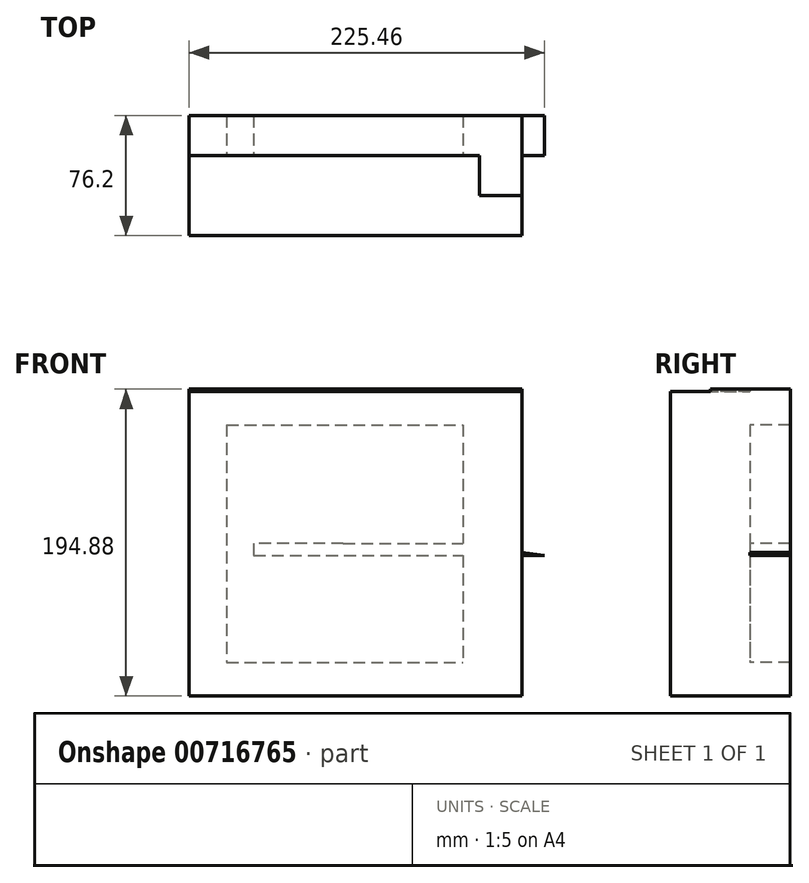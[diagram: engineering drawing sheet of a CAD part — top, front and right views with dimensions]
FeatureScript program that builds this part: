
annotation { "Feature Type Name" : "Feature", "Feature Type Description" : "" }
export const myFeature = defineFeature(function(context is Context, id is Id, definition is map)
    precondition{}
    {
        {
            var Q0;
            Q0=qCreatedBy(makeId("Front.planeOp"),FACE);
            var sketch = newSketch(context, id + "F0", { "sketchPlane" : qUnion([Q0])});
            skLineSegment(sketch, "E0.bottom", {"start": v(-97.79, 96.41) * mm, "end": v(96, 96.41) * mm});
            skLineSegment(sketch, "E0.top", {"start": v(-97.79, -96.95) * mm, "end": v(96, -96.95) * mm});
            skLineSegment(sketch, "E0.left", {"start": v(-97.79, 96.41) * mm, "end": v(-97.79, -96.95) * mm});
            skLineSegment(sketch, "E0.right", {"start": v(96, 96.41) * mm, "end": v(96, -96.95) * mm});
            skSolve(sketch);
        }
        {
            var Q0;
            Q0 = qSketchRegion(id + "F0", true);
            extrude(context, id + "F1", {"entities" : qUnion([Q0]), "depth" : 25.4 * mm, "offsetDistance" : 25.4 * mm});
        }
        {
            var Q0;
            Q0=makeQuery(id+"F1.opExtrude","CAP_FACE",FACE,{"disambiguationData":[OSD([sQuery(id+"F0.wireOp",EDGE,"E0.bottom"),sQuery(id+"F0.wireOp",EDGE,"E0.top"),sQuery(id+"F0.wireOp",EDGE,"E0.left"),sQuery(id+"F0.wireOp",EDGE,"E0.right")])],"isStart":false});
            var sketch = newSketch(context, id + "F2", { "sketchPlane" : qUnion([Q0])});
            skLineSegment(sketch, "E1.bottom", {"start": v(-97.79, -96.95) * mm, "end": v(88.13, -96.95) * mm});
            skLineSegment(sketch, "E1.top", {"start": v(-97.79, 96.41) * mm, "end": v(88.13, 96.41) * mm});
            skLineSegment(sketch, "E1.left", {"start": v(-97.79, -96.95) * mm, "end": v(-97.79, 96.41) * mm});
            skLineSegment(sketch, "E1.right", {"start": v(88.13, -96.95) * mm, "end": v(88.13, 96.41) * mm});
            skSolve(sketch);
        }
        {
            var Q0;
            Q0 = qSketchRegion(id + "F2", true);
            extrude(context, id + "F3", {"entities" : qUnion([Q0]), "operationType" : NewBodyOperationType.ADD, "depth" : 25.4 * mm, "offsetDistance" : 25.4 * mm});
        }
        {
            var Q0;
            Q0=makeQuery(id+"F3.opExtrude","SWEPT_FACE",FACE,{"disambiguationData":[OSD([sQuery(id+"F2.wireOp",EDGE,"E1.right")])]});
            var sketch = newSketch(context, id + "F4", { "sketchPlane" : qUnion([Q0])});
            skLineSegment(sketch, "E2.bottom", {"start": v(-50.8, 96.41) * mm, "end": v(-25.4, 96.41) * mm});
            skLineSegment(sketch, "E2.top", {"start": v(-50.8, -96.95) * mm, "end": v(-25.4, -96.95) * mm});
            skLineSegment(sketch, "E2.left", {"start": v(-50.8, 96.41) * mm, "end": v(-50.8, -96.95) * mm});
            skLineSegment(sketch, "E2.right", {"start": v(-25.4, 96.41) * mm, "end": v(-25.4, -96.95) * mm});
            skSolve(sketch);
        }
        {
            var Q0;
            Q0 = qSketchRegion(id + "F4", true);
            extrude(context, id + "F5", {"entities" : qUnion([Q0]), "operationType" : NewBodyOperationType.ADD, "depth" : 25.4 * mm, "offsetDistance" : 25.4 * mm});
        }
        {
            var Q0;
            Q0=makeQuery(id+"F5.opExtrude","SWEPT_FACE",FACE,{"disambiguationData":[OSD([sQuery(id+"F4.wireOp",EDGE,"E2.right")])]});
            var sketch = newSketch(context, id + "F6", { "sketchPlane" : qUnion([Q0])});
            skLineSegment(sketch, "E3.bottom", {"start": v(-86.6, 97.93) * mm, "end": v(-113.53, 97.93) * mm});
            skLineSegment(sketch, "E3.top", {"start": v(-86.6, -96.95) * mm, "end": v(-113.53, -96.95) * mm});
            skLineSegment(sketch, "E3.left", {"start": v(-86.6, 97.93) * mm, "end": v(-86.6, -96.95) * mm});
            skLineSegment(sketch, "E3.right", {"start": v(-113.53, 97.93) * mm, "end": v(-113.53, -96.95) * mm});
            skSolve(sketch);
        }
        {
            var Q0;
            Q0 = qSketchRegion(id + "F6", true);
            extrude(context, id + "F7", {"entities" : qUnion([Q0]), "operationType" : NewBodyOperationType.ADD, "depth" : 25.4 * mm, "offsetDistance" : 25.4 * mm});
        }
        {
            var Q0;
            Q0=makeQuery(id+"F7.boolean.opBoolean","MERGE",FACE,{"derivedFrom":[makeQuery(id+"F1.opExtrude","CAP_FACE",FACE,{"disambiguationData":[OSD([sQuery(id+"F0.wireOp",EDGE,"E0.bottom"),sQuery(id+"F0.wireOp",EDGE,"E0.top"),sQuery(id+"F0.wireOp",EDGE,"E0.left"),sQuery(id+"F0.wireOp",EDGE,"E0.right")])],"isStart":true}),makeQuery(id+"F7.opExtrude","CAP_FACE",FACE,{"disambiguationData":[OSD([sQuery(id+"F6.wireOp",EDGE,"E3.bottom"),sQuery(id+"F6.wireOp",EDGE,"E3.top"),sQuery(id+"F6.wireOp",EDGE,"E3.left"),sQuery(id+"F6.wireOp",EDGE,"E3.right")])],"isStart":false})]});
            var sketch = newSketch(context, id + "F8", { "sketchPlane" : qUnion([Q0])});
            skLineSegment(sketch, "E4.bottom", {"start": v(74.1, 75.2) * mm, "end": v(-76.06, 75.2) * mm});
            skLineSegment(sketch, "E4.top", {"start": v(74.1, -75.63) * mm, "end": v(-76.06, -75.63) * mm});
            skLineSegment(sketch, "E4.left", {"start": v(74.1, 75.2) * mm, "end": v(74.1, -75.63) * mm});
            skLineSegment(sketch, "E4.right", {"start": v(-76.06, 75.2) * mm, "end": v(-76.06, -75.63) * mm});
            skLineSegment(sketch, "E5.bottom", {"start": v(-113.53, 97.93) * mm, "end": v(97.79, 97.93) * mm});
            skLineSegment(sketch, "E5.top", {"start": v(-113.53, -96.95) * mm, "end": v(97.79, -96.95) * mm});
            skLineSegment(sketch, "E5.left", {"start": v(-113.53, 97.93) * mm, "end": v(-113.53, -96.95) * mm});
            skLineSegment(sketch, "E5.right", {"start": v(97.79, 97.93) * mm, "end": v(97.79, -96.95) * mm});
            skSolve(sketch);
        }
        {
            var Q0;
            Q0 = qSketchRegion(id + "F8", true);
            extrude(context, id + "F9", {"entities" : qUnion([Q0]), "operationType" : NewBodyOperationType.ADD, "depth" : 25.4 * mm, "offsetDistance" : 25.4 * mm});
        }
        {
            var Q0;
            Q0=makeQuery(id+"F7.boolean.opBoolean","MERGE",FACE,{"derivedFrom":[makeQuery(id+"F1.opExtrude","CAP_FACE",FACE,{"disambiguationData":[OSD([sQuery(id+"F0.wireOp",EDGE,"E0.bottom"),sQuery(id+"F0.wireOp",EDGE,"E0.top"),sQuery(id+"F0.wireOp",EDGE,"E0.left"),sQuery(id+"F0.wireOp",EDGE,"E0.right")])],"isStart":true}),makeQuery(id+"F7.opExtrude","CAP_FACE",FACE,{"disambiguationData":[OSD([sQuery(id+"F6.wireOp",EDGE,"E3.bottom"),sQuery(id+"F6.wireOp",EDGE,"E3.top"),sQuery(id+"F6.wireOp",EDGE,"E3.left"),sQuery(id+"F6.wireOp",EDGE,"E3.right")])],"isStart":false})]});
            var sketch = newSketch(context, id + "F10", { "sketchPlane" : qUnion([Q0])});
            skLineSegment(sketch, "E6", {"start": v(0, 0) * mm, "end": v(56.88, -0.21) * mm});
            skPoint(sketch, "E6.endSnap0", {"position": v(-76.06, -0.21) * mm});
            skLineSegment(sketch, "E7", {"start": v(56.88, -0.21) * mm, "end": v(56.86, -7.75) * mm});
            skLineSegment(sketch, "E8", {"start": v(56.86, -7.75) * mm, "end": v(-127.67, -7.75) * mm});
            skLineSegment(sketch, "E9", {"start": v(-127.67, -7.75) * mm, "end": v(-76.06, -0.21) * mm});
            skLineSegment(sketch, "E10", {"start": v(0, 0) * mm, "end": v(-76.06, -0.21) * mm});
            skSolve(sketch);
        }
        {
            var Q0;
            Q0 = qSketchRegion(id + "F10", true);
            extrude(context, id + "F11", {"entities" : qUnion([Q0]), "operationType" : NewBodyOperationType.ADD, "depth" : 25.4 * mm, "offsetDistance" : 25.4 * mm});
        }
    });
